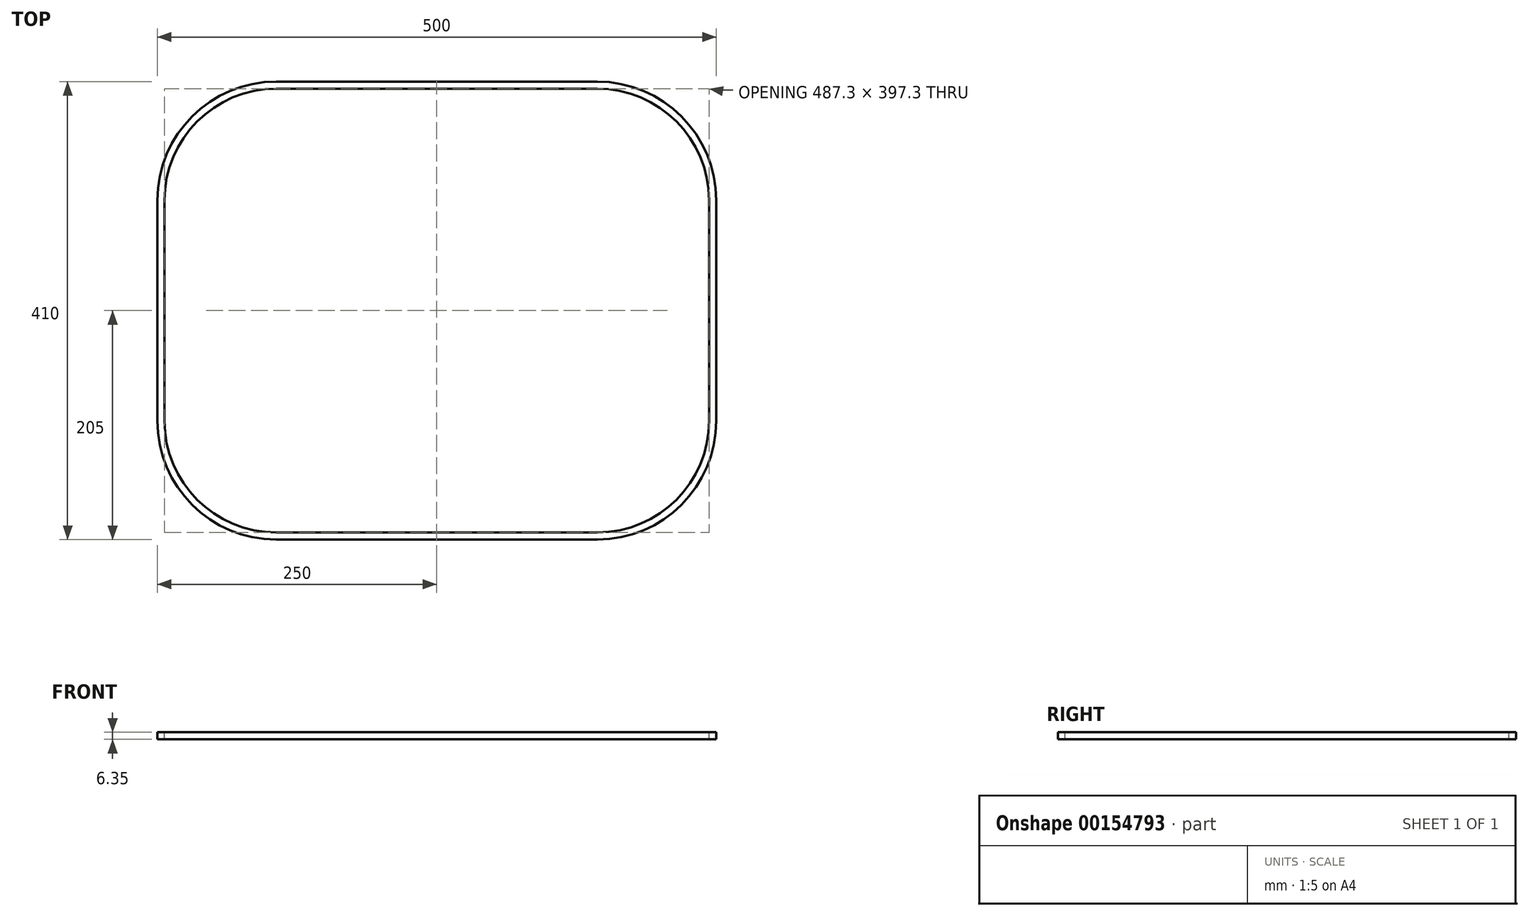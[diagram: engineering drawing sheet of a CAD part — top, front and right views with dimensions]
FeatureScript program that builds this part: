
annotation { "Feature Type Name" : "Feature", "Feature Type Description" : "" }
export const myFeature = defineFeature(function(context is Context, id is Id, definition is map)
    precondition{}
    {
        {
            var Q0;
            Q0=qCreatedBy(makeId("Front.planeOp"),FACE);
            var sketch = newSketch(context, id + "F0", { "sketchPlane" : qUnion([Q0])});
            skLineSegment(sketch, "E0.bottom", {"start": v(0, 0) * mm, "end": v(500, 0) * mm});
            skLineSegment(sketch, "E0.top", {"start": v(0, 6.35) * mm, "end": v(500, 6.35) * mm});
            skLineSegment(sketch, "E0.left", {"start": v(0, 0) * mm, "end": v(0, 6.35) * mm});
            skLineSegment(sketch, "E0.right", {"start": v(500, 0) * mm, "end": v(500, 6.35) * mm});
            skSolve(sketch);
        }
        {
            var Q0;
            Q0 = qSketchRegion(id + "F0", true);
            extrude(context, id + "F1", {"entities" : qUnion([Q0]), "depth" : 410 * mm});
        }
        {
            var Q0;
            Q0=makeQuery(id+"F1.opExtrude","SWEPT_FACE",FACE,{"disambiguationData":[OSD([sQuery(id+"F0.wireOp",EDGE,"E0.top")])]});
            var sketch = newSketch(context, id + "F2", { "sketchPlane" : qUnion([Q0])});
            skLineSegment(sketch, "E1.bottom", {"start": v(106.35, -6.35) * mm, "end": v(393.65, -6.35) * mm});
            skLineSegment(sketch, "E1.top", {"start": v(106.35, -403.65) * mm, "end": v(393.65, -403.65) * mm});
            skLineSegment(sketch, "E1.left", {"start": v(6.35, -106.35) * mm, "end": v(6.35, -303.65) * mm});
            skLineSegment(sketch, "E1.right", {"start": v(493.65, -106.35) * mm, "end": v(493.65, -303.65) * mm});
            skPoint(sketch, "E2.visualSharp", {"position": v(6.35, -6.35) * mm});
            skArc(sketch, "E2.filletArc", {"start": v(106.35, -6.35) * mm, "mid": v(35.64, -35.64) * mm, "end": v(6.35, -106.35) * mm});
            skPoint(sketch, "E3.visualSharp", {"position": v(6.35, -403.65) * mm});
            skArc(sketch, "E3.filletArc", {"start": v(6.35, -303.65) * mm, "mid": v(35.64, -374.36) * mm, "end": v(106.35, -403.65) * mm});
            skPoint(sketch, "E4.visualSharp", {"position": v(493.65, -6.35) * mm});
            skArc(sketch, "E4.filletArc", {"start": v(493.65, -106.35) * mm, "mid": v(464.36, -35.64) * mm, "end": v(393.65, -6.35) * mm});
            skPoint(sketch, "E5.visualSharp", {"position": v(493.65, -403.65) * mm});
            skArc(sketch, "E5.filletArc", {"start": v(393.65, -403.65) * mm, "mid": v(464.36, -374.36) * mm, "end": v(493.65, -303.65) * mm});
            skSolve(sketch);
        }
        {
            var Q0;
            Q0 = qSketchRegion(id + "F2", true);
            extrude(context, id + "F3", {"entities" : qUnion([Q0]), "operationType" : NewBodyOperationType.REMOVE, "oppositeDirection" : true, "depth" : 25 * mm, "offsetDistance" : 25 * mm});
        }
        {
            var Q0;
            Q0=makeQuery(id+"F1.opExtrude","SWEPT_FACE",FACE,{"disambiguationData":[OSD([sQuery(id+"F0.wireOp",EDGE,"E0.top")])]});
            var sketch = newSketch(context, id + "F4", { "sketchPlane" : qUnion([Q0])});
            skLineSegment(sketch, "E6.bottom", {"start": v(106.35, 0) * mm, "end": v(393.65, 0) * mm});
            skLineSegment(sketch, "E6.top", {"start": v(106.35, -410) * mm, "end": v(393.65, -410) * mm});
            skLineSegment(sketch, "E6.left", {"start": v(0, -106.35) * mm, "end": v(0, -303.65) * mm});
            skLineSegment(sketch, "E6.right", {"start": v(500, -106.35) * mm, "end": v(500, -303.65) * mm});
            skPoint(sketch, "E7.visualSharp", {"position": v(0, 0) * mm});
            skArc(sketch, "E7.filletArc", {"start": v(106.35, 0) * mm, "mid": v(31.15, -31.15) * mm, "end": v(0, -106.35) * mm});
            skPoint(sketch, "E8.visualSharp", {"position": v(0, -410) * mm});
            skArc(sketch, "E8.filletArc", {"start": v(0, -303.65) * mm, "mid": v(31.15, -378.85) * mm, "end": v(106.35, -410) * mm});
            skPoint(sketch, "E9.visualSharp", {"position": v(500, -410) * mm});
            skArc(sketch, "E9.filletArc", {"start": v(393.65, -410) * mm, "mid": v(468.85, -378.85) * mm, "end": v(500, -303.65) * mm});
            skPoint(sketch, "E10.visualSharp", {"position": v(500, 0) * mm});
            skArc(sketch, "E10.filletArc", {"start": v(500, -106.35) * mm, "mid": v(468.85, -31.15) * mm, "end": v(393.65, 0) * mm});
            skLineSegment(sketch, "E11.bottom", {"start": v(-8.77, 6.82) * mm, "end": v(508.25, 6.82) * mm});
            skLineSegment(sketch, "E11.top", {"start": v(-8.77, -417.35) * mm, "end": v(508.25, -417.35) * mm});
            skLineSegment(sketch, "E11.left", {"start": v(-8.77, 6.82) * mm, "end": v(-8.77, -417.35) * mm});
            skLineSegment(sketch, "E11.right", {"start": v(508.25, 6.82) * mm, "end": v(508.25, -417.35) * mm});
            skSolve(sketch);
        }
        {
            var Q0;
            Q0 = qSketchRegion(id + "F4", true);
            extrude(context, id + "F5", {"entities" : qUnion([Q0]), "operationType" : NewBodyOperationType.REMOVE, "oppositeDirection" : true, "depth" : 25 * mm, "offsetDistance" : 25 * mm});
        }
    });
